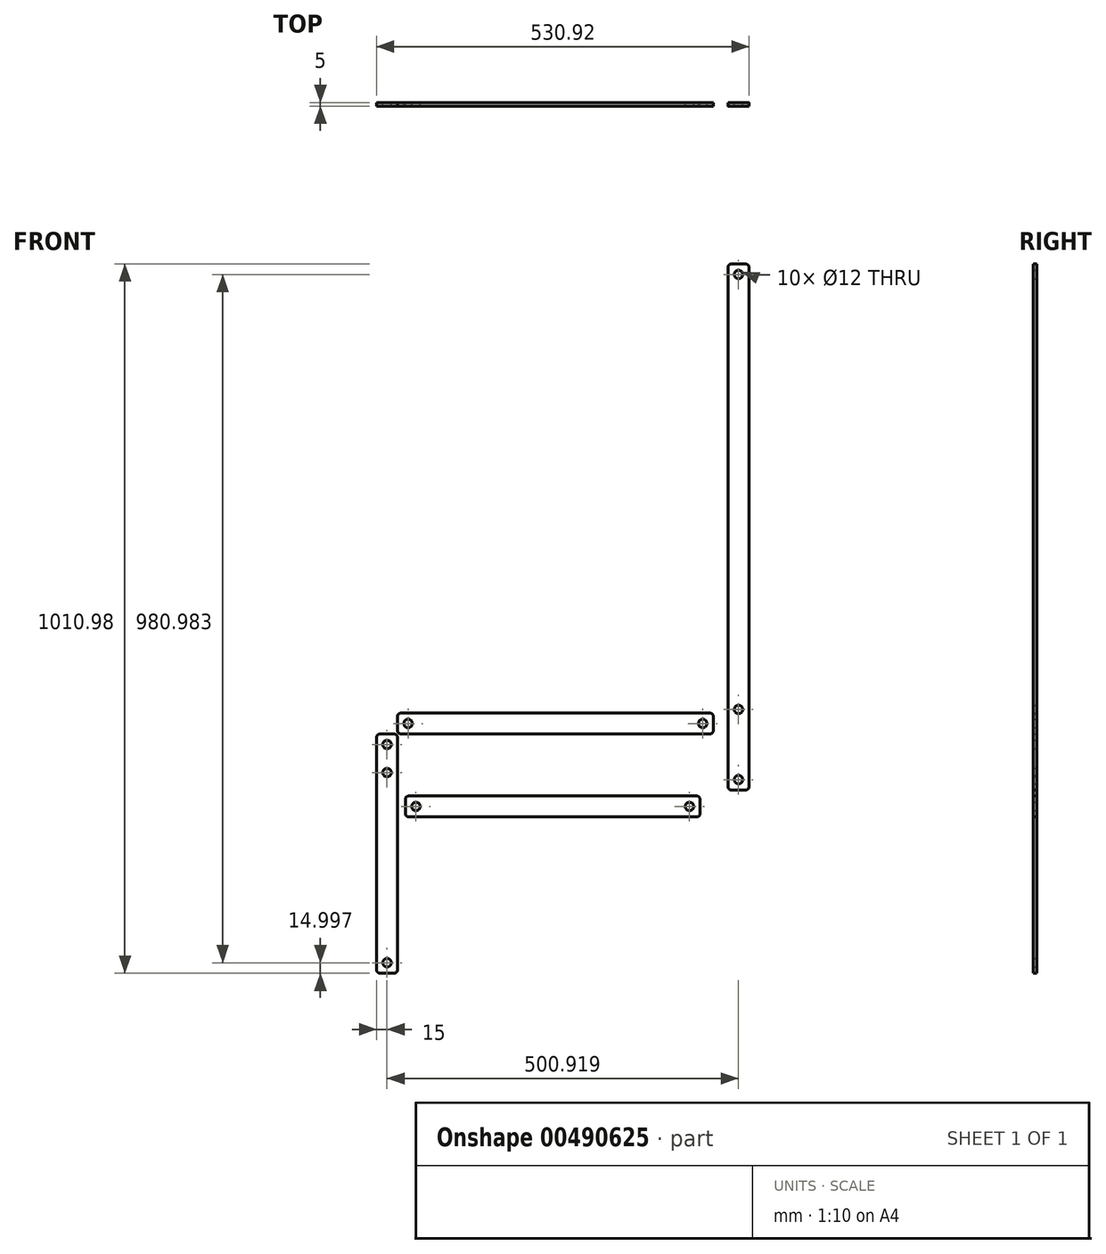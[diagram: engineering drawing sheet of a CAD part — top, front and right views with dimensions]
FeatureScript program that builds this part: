
annotation { "Feature Type Name" : "Feature", "Feature Type Description" : "" }
export const myFeature = defineFeature(function(context is Context, id is Id, definition is map)
    precondition{}
    {
        {
            var Q0;
            Q0=qCreatedBy(makeId("Front.planeOp"),FACE);
            var sketch = newSketch(context, id + "F0", { "sketchPlane" : qUnion([Q0])});
            skLineSegment(sketch, "E0.bottom", {"start": v(5, 0) * mm, "end": v(445, 0) * mm});
            skLineSegment(sketch, "E0.top", {"start": v(5, 30) * mm, "end": v(445, 30) * mm});
            skLineSegment(sketch, "E0.left", {"start": v(0, 5) * mm, "end": v(0, 25) * mm});
            skLineSegment(sketch, "E0.right", {"start": v(450, 5) * mm, "end": v(450, 25) * mm});
            skPoint(sketch, "E1.visualSharp", {"position": v(0, 30) * mm});
            skArc(sketch, "E1.filletArc", {"start": v(5, 30) * mm, "mid": v(1.46, 28.54) * mm, "end": v(0, 25) * mm});
            skPoint(sketch, "E2.visualSharp", {"position": v(0, 0) * mm});
            skArc(sketch, "E2.filletArc", {"start": v(0, 5) * mm, "mid": v(1.46, 1.46) * mm, "end": v(5, 0) * mm});
            skPoint(sketch, "E3.visualSharp", {"position": v(450, 30) * mm});
            skArc(sketch, "E3.filletArc", {"start": v(450, 25) * mm, "mid": v(448.54, 28.54) * mm, "end": v(445, 30) * mm});
            skPoint(sketch, "E4.visualSharp", {"position": v(450, 0) * mm});
            skArc(sketch, "E4.filletArc", {"start": v(445, 0) * mm, "mid": v(448.54, 1.46) * mm, "end": v(450, 5) * mm});
            skCircle(sketch, "E5", {"center": v(15, 15) * mm, "radius": 6 * mm});
            skPoint(sketch, "E5.centerSnap0", {"position": v(0, 15) * mm});
            skCircle(sketch, "E6", {"center": v(435, 15) * mm, "radius": 6 * mm});
            skPoint(sketch, "E6.centerSnap0", {"position": v(450, 15) * mm});
            skSolve(sketch);
        }
        {
            var Q0;
            Q0=makeQuery(id+"F0.imprint","IMPRINT",FACE,{"disambiguationData":[TD([[makeQuery(id+"F0.imprint","IMPRINT",EDGE,{"derivedFrom":sQuery(id+"F0.wireOp",EDGE,"E0.bottom")}),1.0]])]});
            extrude(context, id + "F1", {"entities" : qUnion([Q0]), "depth" : 5 * mm});
        }
        {
            var Q0;
            Q0=qCreatedBy(makeId("Front.planeOp"),FACE);
            var sketch = newSketch(context, id + "F2", { "sketchPlane" : qUnion([Q0])});
            skLineSegment(sketch, "E7.bottom", {"start": v(-5, 0) * mm, "end": v(-25, 0) * mm});
            skLineSegment(sketch, "E7.top", {"start": v(-5, -340.98) * mm, "end": v(-25, -340.98) * mm});
            skLineSegment(sketch, "E7.left", {"start": v(0, -5) * mm, "end": v(0, -335.98) * mm});
            skLineSegment(sketch, "E7.right", {"start": v(-30, -5) * mm, "end": v(-30, -335.98) * mm});
            skPoint(sketch, "E8.visualSharp", {"position": v(-30, 0) * mm});
            skArc(sketch, "E8.filletArc", {"start": v(-25, 0) * mm, "mid": v(-28.54, -1.46) * mm, "end": v(-30, -5) * mm});
            skPoint(sketch, "E9.visualSharp", {"position": v(0, 0) * mm});
            skArc(sketch, "E9.filletArc", {"start": v(0, -5) * mm, "mid": v(-1.46, -1.46) * mm, "end": v(-5, 0) * mm});
            skPoint(sketch, "E10.visualSharp", {"position": v(0, -340.98) * mm});
            skArc(sketch, "E10.filletArc", {"start": v(-5, -340.98) * mm, "mid": v(-1.46, -339.52) * mm, "end": v(0, -335.98) * mm});
            skPoint(sketch, "E11.visualSharp", {"position": v(-30, -340.98) * mm});
            skArc(sketch, "E11.filletArc", {"start": v(-30, -335.98) * mm, "mid": v(-28.54, -339.52) * mm, "end": v(-25, -340.98) * mm});
            skCircle(sketch, "E12", {"center": v(-15, -15) * mm, "radius": 6 * mm});
            skPoint(sketch, "E12.centerSnap0", {"position": v(-15, 0) * mm});
            skCircle(sketch, "E13", {"center": v(-15, -325.98) * mm, "radius": 6 * mm});
            skPoint(sketch, "E13.centerSnap0", {"position": v(-15, -340.98) * mm});
            skCircle(sketch, "E14", {"center": v(-15, -55) * mm, "radius": 6 * mm});
            skLineSegment(sketch, "E15", {"start": v(-30, -100) * mm, "end": v(0, -100) * mm});
            skLineSegment(sketch, "E16", {"start": v(-30, -100) * mm, "end": v(48.18, -335.63) * mm});
            skSolve(sketch);
        }
        {
            var Q0;
            Q0 = qSketchRegion(id + "F2", true);
            extrude(context, id + "F3", {"entities" : qUnion([Q0]), "depth" : 5 * mm});
        }
        {
            var Q0;
            Q0=qCreatedBy(makeId("Front.planeOp"),FACE);
            var sketch = newSketch(context, id + "F4", { "sketchPlane" : qUnion([Q0])});
            skLineSegment(sketch, "E17.bottom", {"start": v(4452.07, 0) * mm, "end": v(4680.77, 0) * mm});
            skLineSegment(sketch, "E17.top", {"start": v(4452.07, 750) * mm, "end": v(4680.77, 750) * mm});
            skLineSegment(sketch, "E17.left", {"start": v(4452.07, 0) * mm, "end": v(4452.07, 750) * mm});
            skLineSegment(sketch, "E17.right", {"start": v(4680.77, 0) * mm, "end": v(4680.77, 750) * mm});
            skLineSegment(sketch, "E18.bottom", {"start": v(475.92, 0) * mm, "end": v(495.92, 0) * mm});
            skLineSegment(sketch, "E18.top", {"start": v(475.92, 750) * mm, "end": v(495.92, 750) * mm});
            skLineSegment(sketch, "E18.left", {"start": v(470.92, 5) * mm, "end": v(470.92, 745) * mm});
            skLineSegment(sketch, "E18.right", {"start": v(500.92, 5) * mm, "end": v(500.92, 745) * mm});
            skCircle(sketch, "E19", {"center": v(485.92, 15) * mm, "radius": 6 * mm});
            skPoint(sketch, "E19.centerSnap0", {"position": v(485.92, 0) * mm});
            skCircle(sketch, "E20", {"center": v(485.92, 735) * mm, "radius": 6 * mm});
            skPoint(sketch, "E20.centerSnap0", {"position": v(485.92, 750) * mm});
            skPoint(sketch, "E21.visualSharp", {"position": v(470.92, 0) * mm});
            skArc(sketch, "E21.filletArc", {"start": v(470.92, 5) * mm, "mid": v(472.38, 1.46) * mm, "end": v(475.92, 0) * mm});
            skPoint(sketch, "E22.visualSharp", {"position": v(500.92, 0) * mm});
            skArc(sketch, "E22.filletArc", {"start": v(495.92, 0) * mm, "mid": v(499.45, 1.46) * mm, "end": v(500.92, 5) * mm});
            skPoint(sketch, "E23.visualSharp", {"position": v(500.92, 750) * mm});
            skArc(sketch, "E23.filletArc", {"start": v(500.92, 745) * mm, "mid": v(499.45, 748.54) * mm, "end": v(495.92, 750) * mm});
            skPoint(sketch, "E24.visualSharp", {"position": v(470.92, 750) * mm});
            skArc(sketch, "E24.filletArc", {"start": v(475.92, 750) * mm, "mid": v(472.38, 748.54) * mm, "end": v(470.92, 745) * mm});
            skCircle(sketch, "E25", {"center": v(485.92, 115) * mm, "radius": 6 * mm});
            skSolve(sketch);
        }
        {
            var Q0;
            Q0=makeQuery(id+"F4.imprint","IMPRINT",FACE,{"disambiguationData":[TD([[makeQuery(id+"F4.imprint","IMPRINT",EDGE,{"derivedFrom":sQuery(id+"F4.wireOp",EDGE,"E18.bottom")}),1.0]])]});
            extrude(context, id + "F5", {"entities" : qUnion([Q0]), "depth" : 5 * mm});
        }
        {
            var Q0;
            Q0=makeQuery(id+"F5.opExtrude","SWEPT_BODY",BODY,{"disambiguationData":[OSD([sQuery(id+"F4.wireOp",EDGE,"E18.bottom"),sQuery(id+"F4.wireOp",EDGE,"E18.top"),sQuery(id+"F4.wireOp",EDGE,"E18.left"),sQuery(id+"F4.wireOp",EDGE,"E18.right"),sQuery(id+"F4.wireOp",EDGE,"E19"),sQuery(id+"F4.wireOp",EDGE,"E20"),sQuery(id+"F4.wireOp",EDGE,"E21.filletArc"),sQuery(id+"F4.wireOp",EDGE,"E22.filletArc"),sQuery(id+"F4.wireOp",EDGE,"E23.filletArc"),sQuery(id+"F4.wireOp",EDGE,"E24.filletArc"),sQuery(id+"F4.wireOp",EDGE,"E25")])]});
            transform(context, id + "F6", {"entities" : qUnion([Q0]), "transformType" : TransformType.TRANSLATION_3D, "dx" : 0 * mm, "dy" : 0 * mm, "dz" : -80 * mm, "makeCopy" : false});
        }
        {
            var Q0;
            Q0=qCreatedBy(makeId("Front.planeOp"),FACE);
            var sketch = newSketch(context, id + "F7", { "sketchPlane" : qUnion([Q0])});
            skLineSegment(sketch, "E26.bottom", {"start": v(16.15, -88.28) * mm, "end": v(426.15, -88.28) * mm});
            skLineSegment(sketch, "E26.top", {"start": v(16.15, -118.28) * mm, "end": v(426.15, -118.28) * mm});
            skLineSegment(sketch, "E26.left", {"start": v(11.15, -93.28) * mm, "end": v(11.15, -113.28) * mm});
            skLineSegment(sketch, "E26.right", {"start": v(431.15, -93.28) * mm, "end": v(431.15, -113.28) * mm});
            skCircle(sketch, "E27", {"center": v(26.15, -103.28) * mm, "radius": 6 * mm});
            skPoint(sketch, "E27.centerSnap0", {"position": v(11.15, -103.28) * mm});
            skCircle(sketch, "E28", {"center": v(416.15, -103.28) * mm, "radius": 6 * mm});
            skPoint(sketch, "E28.centerSnap0", {"position": v(431.15, -103.28) * mm});
            skPoint(sketch, "E29.visualSharp", {"position": v(11.15, -88.28) * mm});
            skArc(sketch, "E29.filletArc", {"start": v(16.15, -88.28) * mm, "mid": v(12.6, -89.74) * mm, "end": v(11.15, -93.28) * mm});
            skPoint(sketch, "E30.visualSharp", {"position": v(11.15, -118.28) * mm});
            skArc(sketch, "E30.filletArc", {"start": v(11.15, -113.28) * mm, "mid": v(12.6, -116.81) * mm, "end": v(16.15, -118.28) * mm});
            skPoint(sketch, "E31.visualSharp", {"position": v(431.15, -88.28) * mm});
            skArc(sketch, "E31.filletArc", {"start": v(431.15, -93.28) * mm, "mid": v(429.68, -89.74) * mm, "end": v(426.15, -88.28) * mm});
            skPoint(sketch, "E32.visualSharp", {"position": v(431.15, -118.28) * mm});
            skArc(sketch, "E32.filletArc", {"start": v(426.15, -118.28) * mm, "mid": v(429.68, -116.81) * mm, "end": v(431.15, -113.28) * mm});
            skSolve(sketch);
        }
        {
            var Q0;
            Q0 = qSketchRegion(id + "F7", true);
            extrude(context, id + "F8", {"entities" : qUnion([Q0]), "depth" : 5 * mm});
        }
    });
